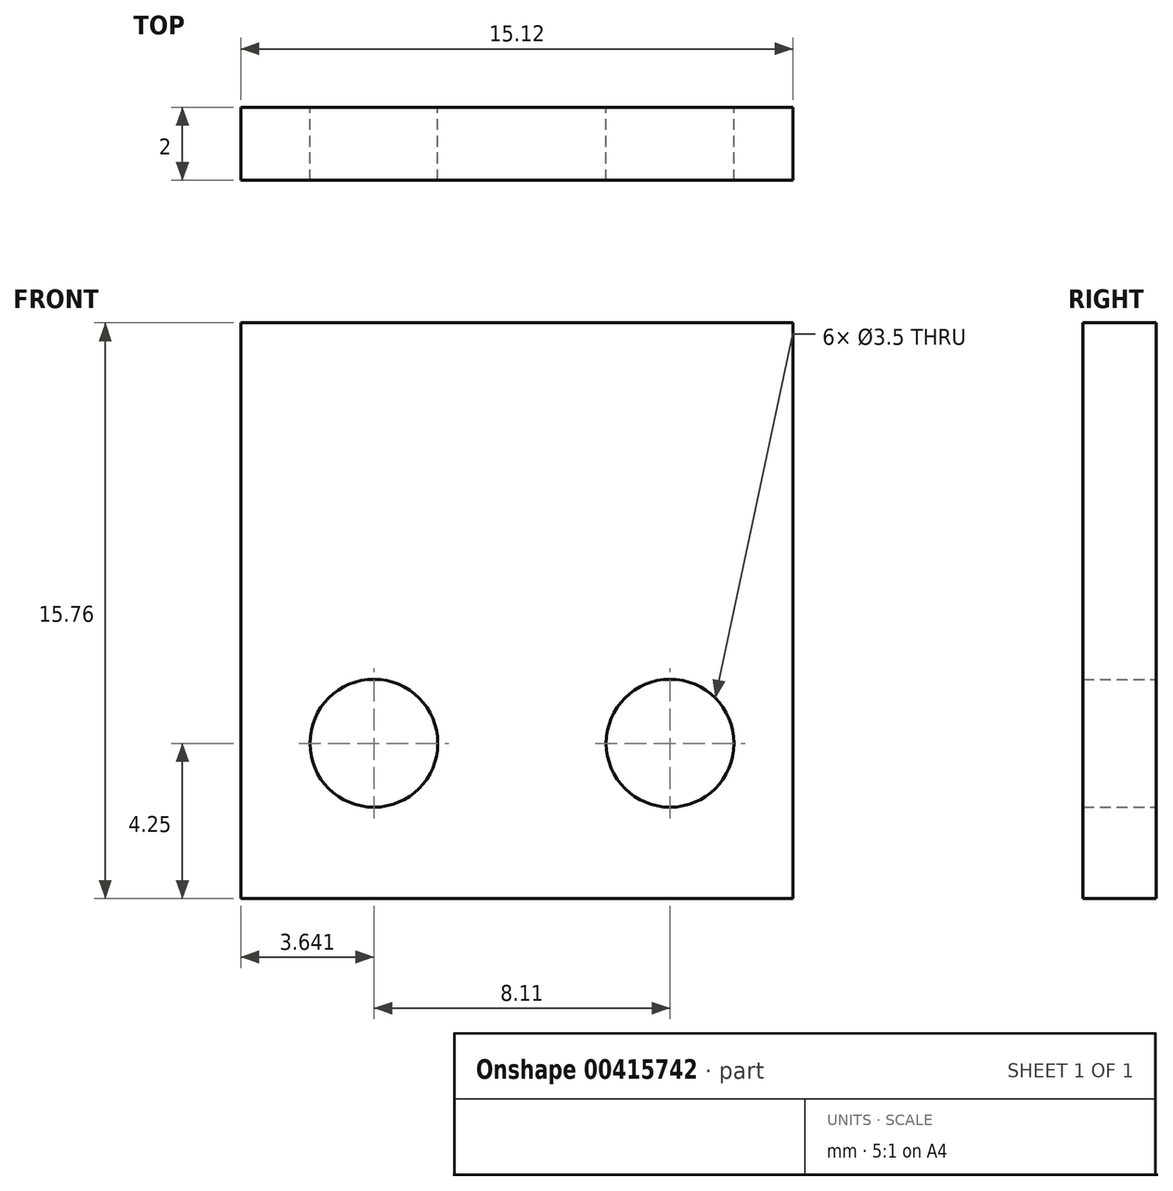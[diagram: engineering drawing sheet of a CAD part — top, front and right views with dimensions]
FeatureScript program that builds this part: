
annotation { "Feature Type Name" : "Feature", "Feature Type Description" : "" }
export const myFeature = defineFeature(function(context is Context, id is Id, definition is map)
    precondition{}
    {
        {
            var Q0;
            Q0=qCreatedBy(makeId("Front.planeOp"),FACE);
            var sketch = newSketch(context, id + "F0", { "sketchPlane" : qUnion([Q0])});
            skLineSegment(sketch, "E0.bottom", {"start": v(-7.56, 7.88) * mm, "end": v(7.56, 7.88) * mm});
            skLineSegment(sketch, "E0.top", {"start": v(-7.56, -7.88) * mm, "end": v(7.56, -7.88) * mm});
            skLineSegment(sketch, "E0.left", {"start": v(-7.56, 7.88) * mm, "end": v(-7.56, -7.88) * mm});
            skLineSegment(sketch, "E0.right", {"start": v(7.56, 7.88) * mm, "end": v(7.56, -7.88) * mm});
            skCircle(sketch, "E1", {"center": v(-3.92, -3.63) * mm, "radius": 1.75 * mm});
            skCircle(sketch, "E2", {"center": v(4.2, -3.63) * mm, "radius": 1.75 * mm});
            skSolve(sketch);
        }
        {
            var Q0;
            Q0=makeQuery(id+"F0.imprint","IMPRINT",FACE,{"disambiguationData":[TD([[makeQuery(id+"F0.imprint","IMPRINT",EDGE,{"derivedFrom":sQuery(id+"F0.wireOp",EDGE,"E0.bottom")}),-1.0]])]});
            extrude(context, id + "F1", {"entities" : qUnion([Q0]), "depth" : 2 * mm});
        }
    });
